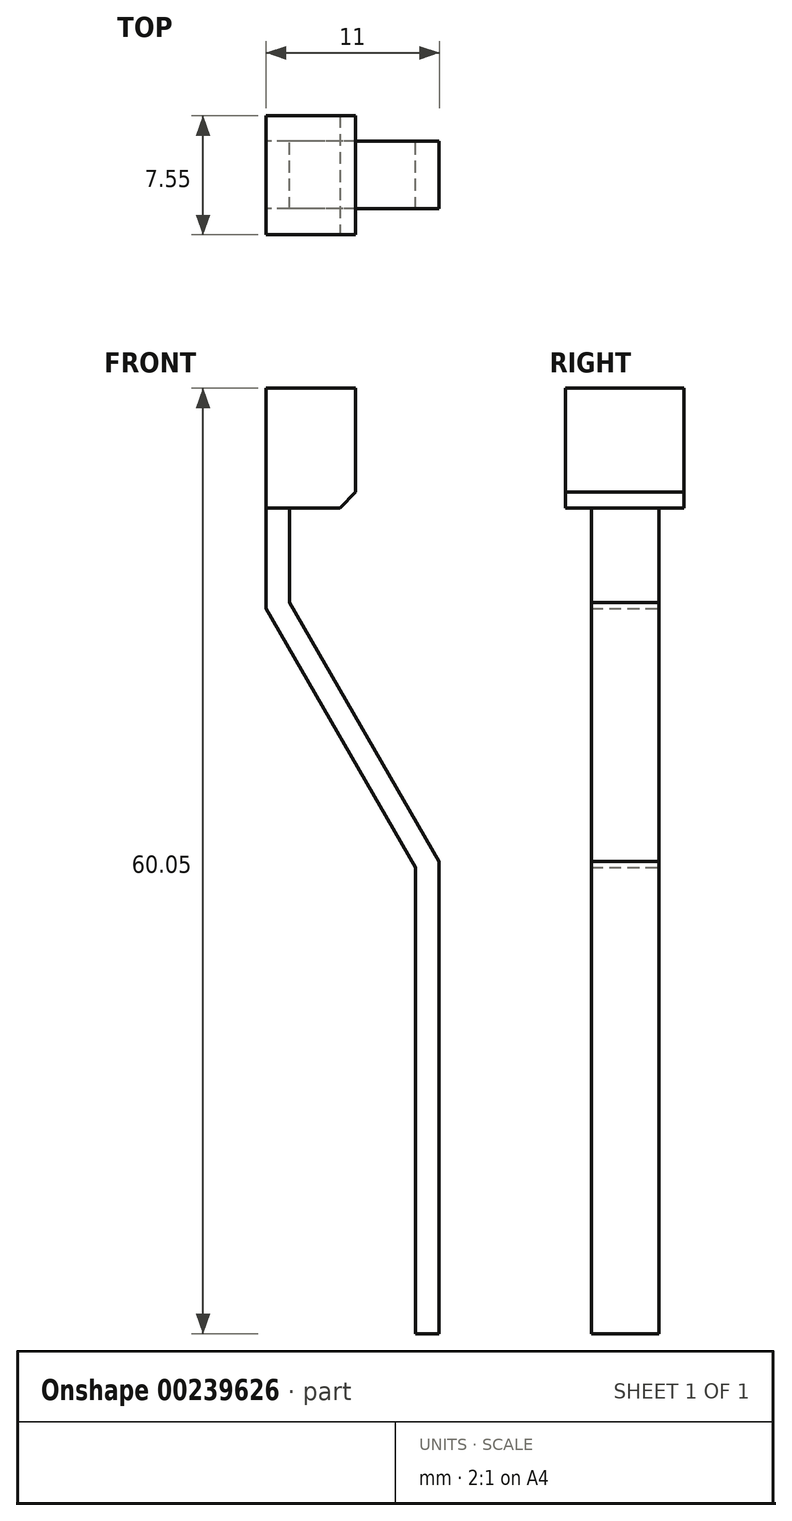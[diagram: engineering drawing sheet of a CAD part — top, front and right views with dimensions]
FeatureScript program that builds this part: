
annotation { "Feature Type Name" : "Feature", "Feature Type Description" : "" }
export const myFeature = defineFeature(function(context is Context, id is Id, definition is map)
    precondition{}
    {
        {
            var Q0;
            Q0=qCreatedBy(makeId("Front.planeOp"),FACE);
            var sketch = newSketch(context, id + "F0", { "sketchPlane" : qUnion([Q0])});
            skLineSegment(sketch, "E0", {"start": v(0, 0) * mm, "end": v(-7.7, 0) * mm});
            skLineSegment(sketch, "E1", {"start": v(-7.7, 0) * mm, "end": v(-7.7, 29.6) * mm});
            skLineSegment(sketch, "E2", {"start": v(-7.7, 29.6) * mm, "end": v(-17.2, 46.05) * mm});
            skLineSegment(sketch, "E3", {"start": v(-6.2, 30) * mm, "end": v(-6.2, 0) * mm});
            skLineSegment(sketch, "E4", {"start": v(-6.2, 0) * mm, "end": v(-7.7, 0) * mm});
            skLineSegment(sketch, "E5", {"start": v(-17.2, 46.05) * mm, "end": v(-17.2, 60.05) * mm});
            skLineSegment(sketch, "E6", {"start": v(-17.2, 60.05) * mm, "end": v(-11.5, 60.05) * mm});
            skLineSegment(sketch, "E7", {"start": v(-11.5, 60.05) * mm, "end": v(-11.5, 52.45) * mm});
            skLineSegment(sketch, "E8", {"start": v(-11.5, 52.45) * mm, "end": v(-15.7, 52.45) * mm});
            skLineSegment(sketch, "E9", {"start": v(-15.7, 52.45) * mm, "end": v(-15.7, 46.45) * mm});
            skLineSegment(sketch, "E10", {"start": v(-6.2, 30) * mm, "end": v(-15.7, 46.45) * mm});
            skSolve(sketch);
        }
        {
            var Q0;
            Q0=qSketchRegion(id+"F0",true);
            extrude(context, id + "F1", {"entities" : qUnion([Q0]), "endBound" : BoundingType.SYMMETRIC, "depth" : 4.3 * mm});
        }
        {
            var Q0;
            Q0=makeQuery(id+"F1.opExtrude","CAP_FACE",FACE,{"disambiguationData":[OSD([sQuery(id+"F0.wireOp",EDGE,"E1"),sQuery(id+"F0.wireOp",EDGE,"E2"),sQuery(id+"F0.wireOp",EDGE,"E3"),sQuery(id+"F0.wireOp",EDGE,"E4"),sQuery(id+"F0.wireOp",EDGE,"E5"),sQuery(id+"F0.wireOp",EDGE,"E6"),sQuery(id+"F0.wireOp",EDGE,"E7"),sQuery(id+"F0.wireOp",EDGE,"E8"),sQuery(id+"F0.wireOp",EDGE,"E9"),sQuery(id+"F0.wireOp",EDGE,"E10")])],"isStart":false});
            var sketch = newSketch(context, id + "F2", { "sketchPlane" : qUnion([Q0])});
            skLineSegment(sketch, "E11", {"start": v(-11.5, 52.45) * mm, "end": v(-17.2, 52.45) * mm});
            skLineSegment(sketch, "E12", {"start": v(-17.2, 52.45) * mm, "end": v(-17.2, 60.05) * mm});
            skLineSegment(sketch, "E13", {"start": v(-17.2, 60.05) * mm, "end": v(-11.5, 60.05) * mm});
            skLineSegment(sketch, "E14", {"start": v(-11.5, 60.05) * mm, "end": v(-11.5, 52.45) * mm});
            skSolve(sketch);
        }
        {
            var Q0;
            Q0=qSketchRegion(id+"F2",true);
            var Q1;
            Q1=makeQuery(id+"F1.opExtrude","CAP_FACE",FACE,{"disambiguationData":[OSD([sQuery(id+"F0.wireOp",EDGE,"E1"),sQuery(id+"F0.wireOp",EDGE,"E2"),sQuery(id+"F0.wireOp",EDGE,"E3"),sQuery(id+"F0.wireOp",EDGE,"E4"),sQuery(id+"F0.wireOp",EDGE,"E5"),sQuery(id+"F0.wireOp",EDGE,"E6"),sQuery(id+"F0.wireOp",EDGE,"E7"),sQuery(id+"F0.wireOp",EDGE,"E8"),sQuery(id+"F0.wireOp",EDGE,"E9"),sQuery(id+"F0.wireOp",EDGE,"E10")])],"isStart":true});
            extrude(context, id + "F3", {"entities" : qUnion([Q0, Q1]), "operationType" : NewBodyOperationType.ADD, "depth" : 1.65 * mm});
        }
        {
            var Q0;
            Q0=makeQuery(id+"F1.opExtrude","CAP_FACE",FACE,{"disambiguationData":[OSD([sQuery(id+"F0.wireOp",EDGE,"E1"),sQuery(id+"F0.wireOp",EDGE,"E2"),sQuery(id+"F0.wireOp",EDGE,"E3"),sQuery(id+"F0.wireOp",EDGE,"E4"),sQuery(id+"F0.wireOp",EDGE,"E5"),sQuery(id+"F0.wireOp",EDGE,"E6"),sQuery(id+"F0.wireOp",EDGE,"E7"),sQuery(id+"F0.wireOp",EDGE,"E8"),sQuery(id+"F0.wireOp",EDGE,"E9"),sQuery(id+"F0.wireOp",EDGE,"E10")])],"isStart":true});
            var sketch = newSketch(context, id + "F4", { "sketchPlane" : qUnion([Q0])});
            skLineSegment(sketch, "E15", {"start": v(17.2, 60.05) * mm, "end": v(11.5, 60.05) * mm});
            skLineSegment(sketch, "E16", {"start": v(11.5, 60.05) * mm, "end": v(11.5, 52.45) * mm});
            skLineSegment(sketch, "E17", {"start": v(11.5, 52.45) * mm, "end": v(17.2, 52.45) * mm});
            skLineSegment(sketch, "E18", {"start": v(17.2, 52.45) * mm, "end": v(17.2, 60.05) * mm});
            skSolve(sketch);
        }
        {
            var Q0;
            Q0=makeQuery(id+"F4.imprint","IMPRINT",FACE,{"disambiguationData":[TD([[makeQuery(id+"F4.imprint","IMPRINT",EDGE,{"derivedFrom":sQuery(id+"F4.wireOp",EDGE,"E15")}),1.0]])]});
            extrude(context, id + "F5", {"entities" : qUnion([Q0]), "operationType" : NewBodyOperationType.ADD, "depth" : 1.6 * mm});
        }
        {
            var Q0;
            Q0=makeQuery(id+"F5.boolean.opBoolean","MERGE",EDGE,{"derivedFrom":[makeQuery(id+"F3.boolean.opBoolean","MERGE",EDGE,{"derivedFrom":[makeQuery(id+"F1.opExtrude","SWEPT_EDGE",EDGE,{"disambiguationData":[OSD([sQuery(id+"F0.wireOp",EDGE,"E7"),sQuery(id+"F0.wireOp",EDGE,"E8")])]}),makeQuery(id+"F3.opExtrude","SWEPT_EDGE",EDGE,{"disambiguationData":[OSD([sQuery(id+"F2.wireOp",EDGE,"E11"),sQuery(id+"F2.wireOp",EDGE,"E14")])]})]}),makeQuery(id+"F5.opExtrude","SWEPT_EDGE",EDGE,{"disambiguationData":[OSD([sQuery(id+"F4.wireOp",EDGE,"E16"),sQuery(id+"F4.wireOp",EDGE,"E17")])]})]});
            chamfer(context, id + "F6", {"entities" : qUnion([Q0]), "width" : 1 * mm, "tangentPropagation" : true});
        }
    });
